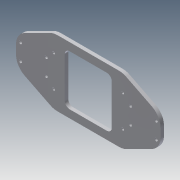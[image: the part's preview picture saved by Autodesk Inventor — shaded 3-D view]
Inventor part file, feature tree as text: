
AUTODESK INVENTOR PART (.ipt)
format: ipt  version: 2014 (Build 180170000, 170)  size: 157,184 bytes
history: native  units: mm
features: extrude x3, sketch x3, fillet x2
ambient origin geometry x8: Origin, YZ Plane, XZ Plane, XY Plane, X Axis, Y Axis, Z Axis, Center Point
bodies: Solid1 (feature_tree)
feature tree (8):
  extrude  "Extrusion1"  Depth=105.0mm
  extrude  "Extrusion2"  Depth=175.0mm
  fillet  "Fillet1"  Radius=87.5mm
  extrude  "Extrusion3"  Depth=8.0mm
  fillet  "Fillet2"  Radius=80.0mm
  sketch  "Sketch1"  dims[d0=105.0mm d3=26.0mm]
  sketch  "Sketch2"  dims[d4=41.0mm d5=175.0mm d6=87.5mm]
  sketch  "Sketch4"  dims[d7=230.0mm d8=4.8mm d9=80.0mm d10=75.0mm d11=5.588mm d12=0.0mm d13=60.0mm d14=30.0mm d15=10.0mm d16=0.0mm d17=25.0mm d18=4.0mm d20=50.0mm d21=10.0mm d22=0.0mm d23=110.0mm d24=8.0mm]
